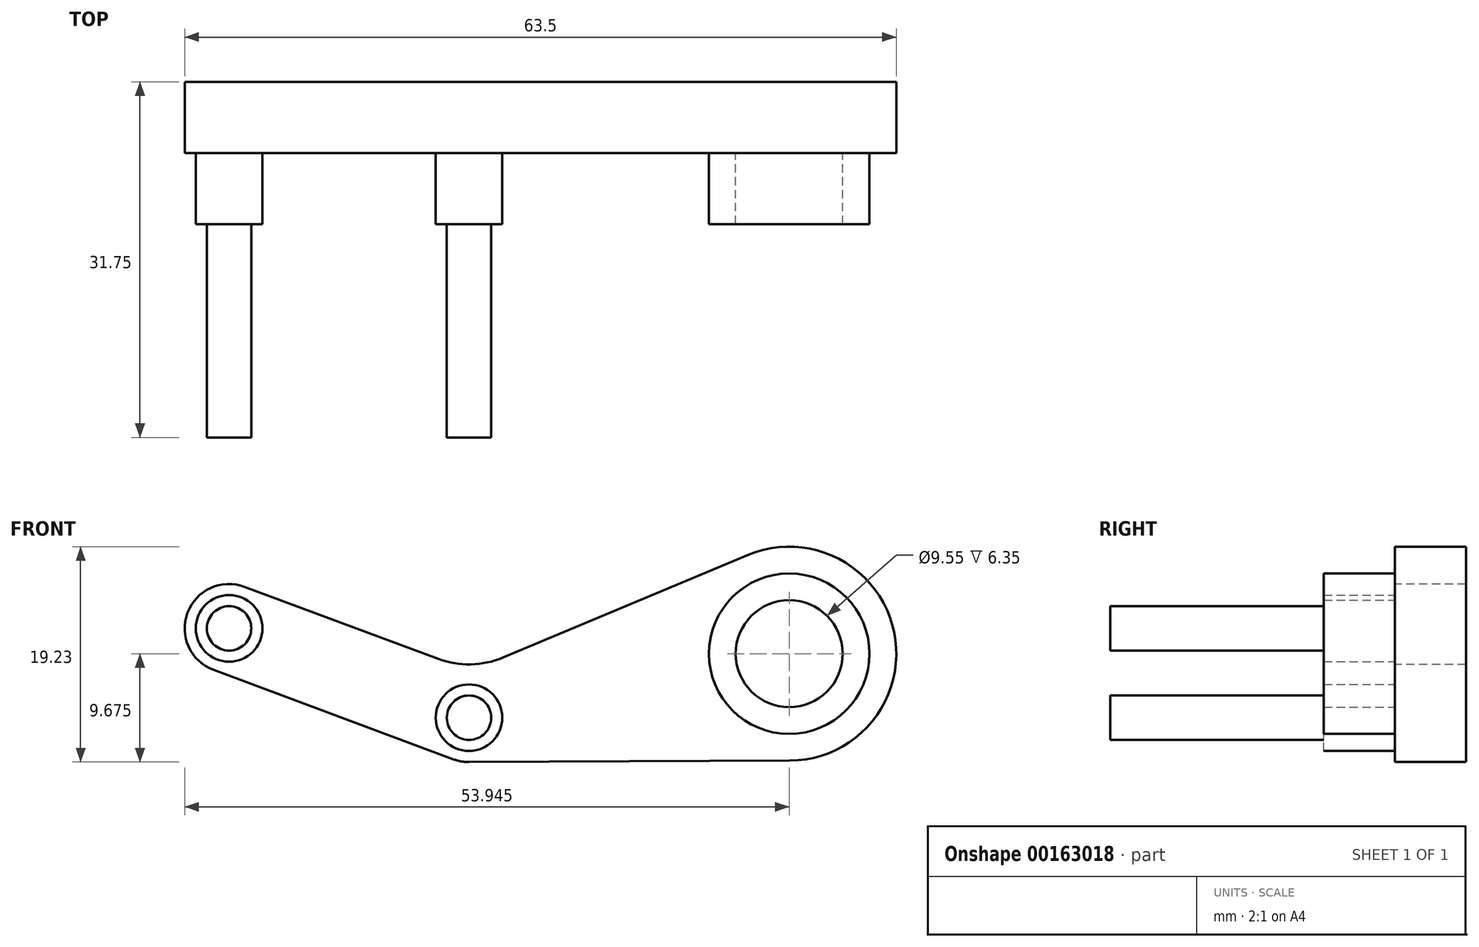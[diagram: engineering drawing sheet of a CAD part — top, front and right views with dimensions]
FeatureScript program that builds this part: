
annotation { "Feature Type Name" : "Feature", "Feature Type Description" : "" }
export const myFeature = defineFeature(function(context is Context, id is Id, definition is map)
    precondition{}
    {
        {
            var Q0;
            Q0=qCreatedBy(makeId("Front.planeOp"),FACE);
            var sketch = newSketch(context, id + "F0", { "sketchPlane" : qUnion([Q0])});
            skPoint(sketch, "E0.middle", {"position": v(0, 0) * mm});
            skCircle(sketch, "E1", {"center": v(-21.41, 7.98) * mm, "radius": 1.98 * mm});
            skCircle(sketch, "E2", {"center": v(0, 0) * mm, "radius": 1.98 * mm});
            skCircle(sketch, "E3", {"center": v(28.58, 5.72) * mm, "radius": 4.78 * mm});
            skCircle(sketch, "E4", {"center": v(-21.41, 7.98) * mm, "radius": 2.97 * mm});
            skCircle(sketch, "E5", {"center": v(0, 0) * mm, "radius": 2.97 * mm});
            skCircle(sketch, "E6", {"center": v(28.58, 5.72) * mm, "radius": 7.16 * mm});
            skLineSegment(sketch, "E7.left", {"start": v(-21.41, 4) * mm, "end": v(-21.41, 3.99) * mm});
            skArc(sketch, "E8", {"start": v(-20.03, 11.69) * mm, "mid": v(-25.13, 9.36) * mm, "end": v(-22.8, 4.26) * mm});
            skArc(sketch, "E9", {"start": v(-1.38, -3.71) * mm, "mid": v(-0.7, -3.9) * mm, "end": v(0.02, -3.96) * mm});
            skArc(sketch, "E10", {"start": v(28.62, -3.84) * mm, "mid": v(37.93, 7.62) * mm, "end": v(24.88, 14.52) * mm});
            skLineSegment(sketch, "E11", {"start": v(-20.03, 11.69) * mm, "end": v(-2.77, 5.26) * mm});
            skLineSegment(sketch, "E12", {"start": v(-22.8, 4.26) * mm, "end": v(-1.38, -3.71) * mm});
            skLineSegment(sketch, "E13", {"start": v(28.62, -3.84) * mm, "end": v(0.02, -3.96) * mm});
            skLineSegment(sketch, "E14", {"start": v(3.06, 5.38) * mm, "end": v(24.88, 14.52) * mm});
            skArc(sketch, "E15.filletArc", {"start": v(-2.77, 5.26) * mm, "mid": v(0.16, 4.76) * mm, "end": v(3.06, 5.38) * mm});
            skSolve(sketch);
        }
        {
            var Q0;
            Q0 = qSketchRegion(id + "F0", true);
            var Q1;
            Q1=makeQuery(id+"F0.imprint","IMPRINT",FACE,{"disambiguationData":[TD([[makeQuery(id+"F0.imprint","IMPRINT",EDGE,{"derivedFrom":sQuery(id+"F0.wireOp",EDGE,"E1")}),-1.0]])]});
            var Q2;
            Q2=makeQuery(id+"F0.imprint","IMPRINT",FACE,{"disambiguationData":[TD([[makeQuery(id+"F0.imprint","IMPRINT",EDGE,{"derivedFrom":sQuery(id+"F0.wireOp",EDGE,"E1")}),1.0]])]});
            var Q3;
            Q3=makeQuery(id+"F0.imprint","IMPRINT",FACE,{"disambiguationData":[TD([[makeQuery(id+"F0.imprint","IMPRINT",EDGE,{"derivedFrom":sQuery(id+"F0.wireOp",EDGE,"E2")}),-1.0]])]});
            var Q4;
            Q4=makeQuery(id+"F0.imprint","IMPRINT",FACE,{"disambiguationData":[TD([[makeQuery(id+"F0.imprint","IMPRINT",EDGE,{"derivedFrom":sQuery(id+"F0.wireOp",EDGE,"E2")}),1.0]])]});
            var Q5;
            Q5=makeQuery(id+"F0.imprint","IMPRINT",FACE,{"disambiguationData":[TD([[makeQuery(id+"F0.imprint","IMPRINT",EDGE,{"derivedFrom":sQuery(id+"F0.wireOp",EDGE,"E3")}),-1.0]])]});
            var Q6;
            Q6=makeQuery(id+"F0.imprint","IMPRINT",FACE,{"disambiguationData":[TD([[makeQuery(id+"F0.imprint","IMPRINT",EDGE,{"derivedFrom":sQuery(id+"F0.wireOp",EDGE,"E3")}),1.0]])]});
            extrude(context, id + "F1", {"entities" : qUnion([Q0, Q1, Q2, Q3, Q4, Q5, Q6]), "oppositeDirection" : true, "depth" : 6.35 * mm});
        }
        {
            var Q0;
            Q0=makeQuery(id+"F0.imprint","IMPRINT",FACE,{"disambiguationData":[TD([[makeQuery(id+"F0.imprint","IMPRINT",EDGE,{"derivedFrom":sQuery(id+"F0.wireOp",EDGE,"E1")}),-1.0]])]});
            var Q1;
            Q1=makeQuery(id+"F0.imprint","IMPRINT",FACE,{"disambiguationData":[TD([[makeQuery(id+"F0.imprint","IMPRINT",EDGE,{"derivedFrom":sQuery(id+"F0.wireOp",EDGE,"E2")}),-1.0]])]});
            var Q2;
            Q2=makeQuery(id+"F0.imprint","IMPRINT",FACE,{"disambiguationData":[TD([[makeQuery(id+"F0.imprint","IMPRINT",EDGE,{"derivedFrom":sQuery(id+"F0.wireOp",EDGE,"E3")}),-1.0]])]});
            extrude(context, id + "F2", {"entities" : qUnion([Q0, Q1, Q2]), "operationType" : NewBodyOperationType.ADD, "depth" : 6.35 * mm});
        }
        {
            var Q0;
            Q0=makeQuery(id+"F0.imprint","IMPRINT",FACE,{"disambiguationData":[TD([[makeQuery(id+"F0.imprint","IMPRINT",EDGE,{"derivedFrom":sQuery(id+"F0.wireOp",EDGE,"E1")}),1.0]])]});
            var Q1;
            Q1=makeQuery(id+"F0.imprint","IMPRINT",FACE,{"disambiguationData":[TD([[makeQuery(id+"F0.imprint","IMPRINT",EDGE,{"derivedFrom":sQuery(id+"F0.wireOp",EDGE,"E2")}),1.0]])]});
            extrude(context, id + "F3", {"entities" : qUnion([Q0, Q1]), "operationType" : NewBodyOperationType.ADD, "depth" : 25.4 * mm});
        }
    });
